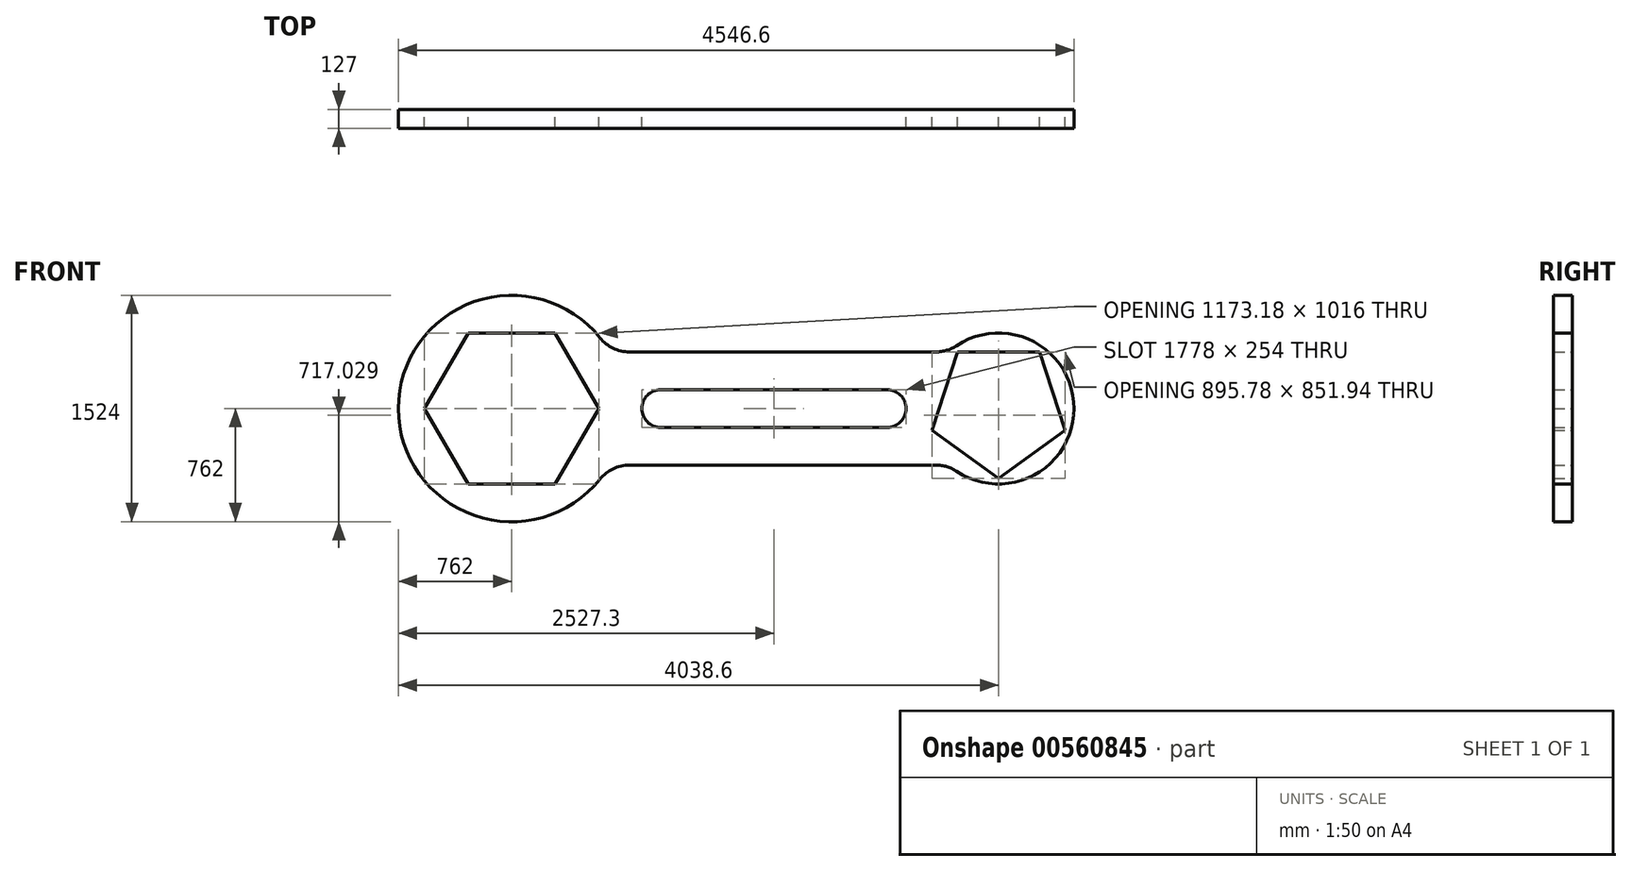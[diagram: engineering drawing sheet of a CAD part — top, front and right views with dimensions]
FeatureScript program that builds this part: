
annotation { "Feature Type Name" : "Feature", "Feature Type Description" : "" }
export const myFeature = defineFeature(function(context is Context, id is Id, definition is map)
    precondition{}
    {
        {
            var Q0;
            Q0=qCreatedBy(makeId("Front.planeOp"),FACE);
            var sketch = newSketch(context, id + "F0", { "sketchPlane" : qUnion([Q0])});
            skCircle(sketch, "E0", {"center": v(0, 0) * mm, "radius": 762 * mm});
            skCircle(sketch, "E1", {"center": v(3276.6, 0) * mm, "radius": 508 * mm});
            skLineSegment(sketch, "E2", {"start": v(762, 0) * mm, "end": v(2768.6, 0) * mm});
            skLineSegment(sketch, "E3", {"start": v(1765.3, 0) * mm, "end": v(1765.3, 127) * mm});
            skLineSegment(sketch, "E4", {"start": v(1003.3, 127) * mm, "end": v(1765.3, 127) * mm});
            skLineSegment(sketch, "E5", {"start": v(1003.3, -127) * mm, "end": v(2527.3, -127) * mm});
            skLineSegment(sketch, "E6", {"start": v(2527.3, 127) * mm, "end": v(1765.3, 127) * mm});
            skLineSegment(sketch, "E7", {"start": v(876.3, 0) * mm, "end": v(1003.3, 0) * mm});
            skCircle(sketch, "E8", {"center": v(1003.3, 0) * mm, "radius": 127 * mm});
            skLineSegment(sketch, "E9", {"start": v(1765.3, -127) * mm, "end": v(1765.3, -381) * mm});
            skLineSegment(sketch, "E10", {"start": v(1765.3, -381) * mm, "end": v(793.11, -381) * mm});
            skLineSegment(sketch, "E11", {"start": v(1765.3, -381) * mm, "end": v(2940.59, -381) * mm});
            skLineSegment(sketch, "E12", {"start": v(1765.3, 127) * mm, "end": v(1765.3, 381) * mm});
            skLineSegment(sketch, "E13", {"start": v(793.11, 381) * mm, "end": v(2855.39, 381) * mm});
            skLineSegment(sketch, "E14", {"start": v(2654.3, 0) * mm, "end": v(2527.3, 0) * mm});
            skCircle(sketch, "E15", {"center": v(2527.3, 0) * mm, "radius": 127 * mm});
            skPoint(sketch, "E16.orphan", {"position": v(876.3, 127) * mm});
            skPoint(sketch, "E17.orphan", {"position": v(876.3, -127) * mm});
            skPoint(sketch, "E18.orphan", {"position": v(2654.3, -127) * mm});
            skPoint(sketch, "E19.orphan", {"position": v(2654.3, 127) * mm});
            skArc(sketch, "E20", {"start": v(594.84, 476.25) * mm, "mid": v(683.13, 406.05) * mm, "end": v(793.11, 381) * mm});
            skPoint(sketch, "E21.orphan", {"position": v(659.91, 381) * mm});
            skArc(sketch, "E22", {"start": v(793.11, -381) * mm, "mid": v(683.13, -406.05) * mm, "end": v(594.84, -476.25) * mm});
            skArc(sketch, "E23", {"start": v(2995.8, -423.33) * mm, "mid": v(2928.71, -391.81) * mm, "end": v(2855.39, -381) * mm});
            skArc(sketch, "E24", {"start": v(2855.39, 381) * mm, "mid": v(2928.71, 391.81) * mm, "end": v(2995.8, 423.33) * mm});
            skCircle(sketch, "E25.cCircle", {"center": v(0, 0) * mm, "radius": 508 * mm, "construction": true});
            skLineSegment(sketch, "E25.0", {"start": v(-293.3, 508) * mm, "end": v(293.3, 508) * mm});
            skLineSegment(sketch, "E25.1", {"start": v(293.3, 508) * mm, "end": v(586.59, 0) * mm});
            skLineSegment(sketch, "E25.2", {"start": v(586.59, 0) * mm, "end": v(293.3, -508) * mm});
            skLineSegment(sketch, "E25.3", {"start": v(293.3, -508) * mm, "end": v(-293.3, -508) * mm});
            skLineSegment(sketch, "E25.4", {"start": v(-293.3, -508) * mm, "end": v(-586.59, 0) * mm});
            skLineSegment(sketch, "E25.5", {"start": v(-586.59, 0) * mm, "end": v(-293.3, 508) * mm});
            skPoint(sketch, "E25.0.midPoint", {"position": v(0, 508) * mm});
            skCircle(sketch, "E26.cCircle", {"center": v(3276.6, 0) * mm, "radius": 381 * mm, "construction": true});
            skLineSegment(sketch, "E26.0", {"start": v(2999.79, 381) * mm, "end": v(3553.41, 381) * mm});
            skLineSegment(sketch, "E26.1", {"start": v(3553.41, 381) * mm, "end": v(3724.5, -145.53) * mm});
            skLineSegment(sketch, "E26.2", {"start": v(3724.5, -145.53) * mm, "end": v(3276.6, -470.94) * mm});
            skLineSegment(sketch, "E26.3", {"start": v(3276.6, -470.94) * mm, "end": v(2828.7, -145.53) * mm});
            skLineSegment(sketch, "E26.4", {"start": v(2828.7, -145.53) * mm, "end": v(2999.79, 381) * mm});
            skPoint(sketch, "E26.0.midPoint", {"position": v(3276.6, 381) * mm});
            skSolve(sketch);
        }
        {
            var Q0;
            {var subQ3=sQuery(id+"F0.wireOp",EDGE,"E23");Q0=makeQuery(id+"F0.imprint","IMPRINT",FACE,{"disambiguationData":[TD([[makeQuery(id+"F0.imprint","IMPRINT",EDGE,{"derivedFrom":subQ3}),-1.0]])]});}
            var Q1;
            Q1=makeQuery(id+"F0.imprint","IMPRINT",FACE,{"disambiguationData":[TD([[makeQuery(id+"F0.imprint","IMPRINT",EDGE,{"derivedFrom":sQuery(id+"F0.wireOp",EDGE,"E25.0")}),1.0]])]});
            var Q2;
            {var subQ0=sQuery(id+"F0.wireOp",EDGE,"E4");Q2=makeQuery(id+"F0.imprint","IMPRINT",FACE,{"disambiguationData":[TD([[makeQuery(id+"F0.imprint","IMPRINT",EDGE,{"derivedFrom":subQ0}),1.0]])]});}
            var Q3;
            {var subQ5=sQuery(id+"F0.wireOp",EDGE,"E9");Q3=makeQuery(id+"F0.imprint","IMPRINT",FACE,{"disambiguationData":[TD([[makeQuery(id+"F0.imprint","IMPRINT",EDGE,{"derivedFrom":subQ5}),-1.0]])]});}
            var Q4;
            {var subQ0=sQuery(id+"F0.wireOp",EDGE,"E9");Q4=makeQuery(id+"F0.imprint","IMPRINT",FACE,{"disambiguationData":[TD([[makeQuery(id+"F0.imprint","IMPRINT",EDGE,{"derivedFrom":subQ0}),1.0]])]});}
            var Q5;
            {var subQ2=sQuery(id+"F0.wireOp",EDGE,"E6");Q5=makeQuery(id+"F0.imprint","IMPRINT",FACE,{"disambiguationData":[TD([[makeQuery(id+"F0.imprint","IMPRINT",EDGE,{"derivedFrom":subQ2}),-1.0]])]});}
            var Q6;
            Q6=makeQuery(id+"F0.imprint","IMPRINT",FACE,{"disambiguationData":[TD([[makeQuery(id+"F0.imprint","IMPRINT",EDGE,{"derivedFrom":sQuery(id+"F0.wireOp",EDGE,"E26.0")}),1.0]])]});
            extrude(context, id + "F1", {"entities" : qUnion([Q0, Q1, Q2, Q3, Q4, Q5, Q6]), "depth" : 127 * mm, "offsetDistance" : 25.4 * mm});
        }
    });
